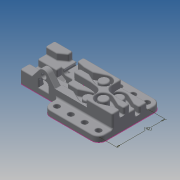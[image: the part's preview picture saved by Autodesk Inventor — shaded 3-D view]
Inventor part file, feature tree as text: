
AUTODESK INVENTOR PART (.ipt)
format: ipt  version: 2014 (Build 180170000, 170)  size: 1,244,672 bytes
history: native  units: mm
features: sketch x21, extrude x19, fillet x13, mirror x1
ambient origin geometry x8: Origin, YZ Plane, XZ Plane, XY Plane, X Axis, Y Axis, Z Axis, Center Point
bodies: Solid1 (feature_tree)
feature tree (54):
  extrude  "Extrusion1"  Depth=40.0mm
  extrude  "Extrusion2"  Depth=80.0mm
  extrude  "Extrusion3"  Depth=26.52mm
  extrude  "Extrusion4"  Depth=10.0mm
  extrude  "Extrusion5"  Depth=8.26mm
  extrude  "Extrusion6"  Depth=6.0mm TaperAngle=0.0deg
  extrude  "Extrusion7"  Depth=4.0mm
  extrude  "Extrusion8"  Depth=8.0mm
  extrude  "Extrusion9"  Depth=3.0mm
  extrude  "Extrusion10"  Depth=9.0mm
  extrude  "Extrusion11"  Depth=6.0mm TaperAngle=0.0deg
  sketch  "Sketch12"  dims[d29=5.0mm d31=6.0mm d32=0.0mm]
  extrude  "Extrusion12"  Depth=6.0mm TaperAngle=0.0deg
  extrude  "Extrusion13"  Depth=6.0mm TaperAngle=0.0deg
  extrude  "Extrusion14"  Depth=6.0mm TaperAngle=0.0deg
  extrude  "Extrusion16"  Depth=6.0mm TaperAngle=0.0deg
  extrude  "Extrusion17"  Depth=6.0mm TaperAngle=0.0deg
  mirror  "Mirror1"
  extrude  "Extrusion18"  Depth=3.5mm
  extrude  "Extrusion19"  Depth=17.75mm TaperAngle=0.0deg
  extrude  "Extrusion20"  Depth=4.5mm
  fillet  "Fillet1"  Radius=4.1mm
  fillet  "Fillet2"  Radius=3.0mm
  fillet  "Fillet3"  Radius=20.0mm
  fillet  "Fillet4"  Radius=5.0mm
  fillet  "Fillet5"  Radius=4.6mm
  fillet  "Fillet6"  Radius=12.0mm
  fillet  "Fillet7"  Radius=6.0mm
  fillet  "Fillet9"  Radius=6.0mm
  fillet  "Fillet10"  Radius=5.0mm
  fillet  "Fillet11"  Radius=1.5mm
  fillet  "Fillet12"  Radius=1.5mm
  fillet  "Fillet13"  Radius=1.0mm
  sketch  "Sketch22"  dims[d75=0.5mm d76=0.5mm d77=0.2mm d78=7.2mm d79=6.0mm d80=0.0mm d81=4.0mm d82=0.0mm d83=7.0mm d84=6.0mm d85=0.0mm d86=2.0mm d87=1.0mm d88=1.0mm d89=1.0mm d90=0.5mm d91=42.0mm]
  fillet  "Fillet8"  Radius=1.0mm
  sketch  "Sketch1"  dims[d0=26.52mm d1=40.0mm]
  sketch  "Sketch2"  dims[d2=30.0mm d3=80.0mm]
  sketch  "Sketch3"  dims[d4=5.0mm d5=0.0mm d6=26.52mm]
  sketch  "Sketch4"  dims[d7=40.0mm d8=10.0mm]
  sketch  "Sketch5"  dims[d9=6.0mm d10=0.0mm d13=8.26mm]
  sketch  "Sketch6"  dims[d14=8.26mm d15=6.0mm d16=0.0mm]
  sketch  "Sketch7"  dims[d17=6.0mm d18=4.0mm]
  sketch  "Sketch8"  dims[d19=6.0mm d20=0.0mm d21=8.0mm]
  sketch  "Sketch9"  dims[d22=12.0mm d23=3.0mm]
  sketch  "Sketch10"  dims[d24=11.0mm d25=9.0mm]
  sketch  "Sketch11"  dims[d26=8.0mm d27=6.0mm d28=0.0mm]
  sketch  "Sketch13"  dims[d34=25.0mm d35=6.0mm d36=0.0mm]
  sketch  "Sketch14"  dims[d37=6.0mm d38=0.0mm d40=6.0mm d41=0.0mm]
  sketch  "Sketch15"  dims[d42=6.0mm d43=0.0mm d44=6.0mm d45=0.0mm]
  sketch  "Sketch17"  dims[d46=11.0mm d47=6.0mm d48=0.0mm]
  sketch  "Sketch18"  dims[d49=6.0mm d50=0.0mm d51=3.5mm]
  sketch  "Sketch19"  dims[d52=4.15mm d53=17.75mm d54=0.0mm]
  sketch  "Sketch20"  dims[d55=1.75mm d58=4.5mm d59=4.1mm d60=3.0mm d61=20.0mm d62=5.0mm d63=0.0mm d64=4.6mm d65=12.0mm d66=6.0mm d67=6.0mm d68=5.0mm d69=0.0mm d70=1.5mm d71=1.5mm d72=1.0mm d73=1.0mm]
  sketch  "Sketch21"  dims[d74=1.0mm]
